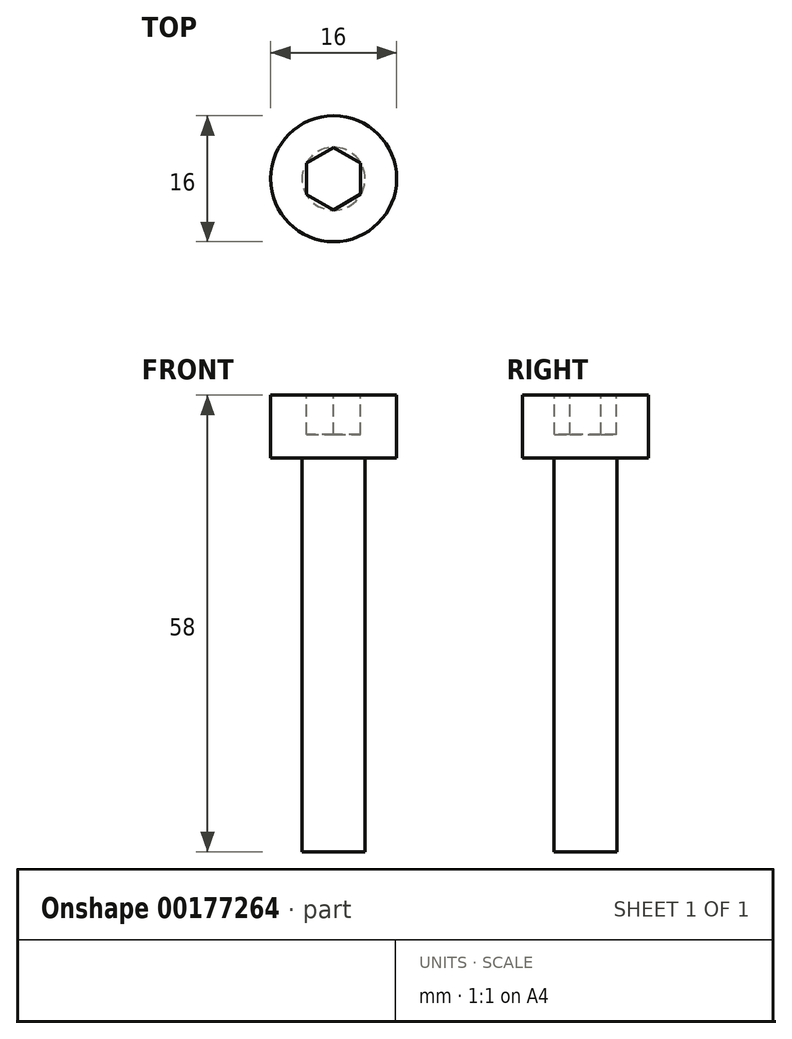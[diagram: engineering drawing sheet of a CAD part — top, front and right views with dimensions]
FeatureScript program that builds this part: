
annotation { "Feature Type Name" : "Feature", "Feature Type Description" : "" }
export const myFeature = defineFeature(function(context is Context, id is Id, definition is map)
    precondition{}
    {
        {
            var Q0;
            Q0=qCreatedBy(makeId("Top.planeOp"),FACE);
            var sketch = newSketch(context, id + "F0", { "sketchPlane" : qUnion([Q0])});
            skCircle(sketch, "E0", {"center": v(0, 0) * mm, "radius": 4 * mm});
            skCircle(sketch, "E1", {"center": v(0, 0) * mm, "radius": 8 * mm});
            skSolve(sketch);
        }
        {
            var Q0;
            Q0=makeQuery(id+"F0.imprint","IMPRINT",FACE,{"disambiguationData":[TD([[makeQuery(id+"F0.imprint","IMPRINT",EDGE,{"derivedFrom":sQuery(id+"F0.wireOp",EDGE,"E0")}),1.0]])]});
            extrude(context, id + "F1", {"entities" : qUnion([Q0]), "oppositeDirection" : true, "depth" : 50 * mm});
        }
        {
            var Q0;
            Q0=makeQuery(id+"F0.imprint","IMPRINT",FACE,{"disambiguationData":[TD([[makeQuery(id+"F0.imprint","IMPRINT",EDGE,{"derivedFrom":sQuery(id+"F0.wireOp",EDGE,"E0")}),-1.0]])]});
            var Q1;
            Q1=makeQuery(id+"F0.imprint","IMPRINT",FACE,{"disambiguationData":[TD([[makeQuery(id+"F0.imprint","IMPRINT",EDGE,{"derivedFrom":sQuery(id+"F0.wireOp",EDGE,"E0")}),1.0]])]});
            extrude(context, id + "F2", {"entities" : qUnion([Q0, Q1]), "operationType" : NewBodyOperationType.ADD, "depth" : 8 * mm});
        }
        {
            var Q0;
            Q0=makeQuery(id+"F2.opExtrude","CAP_FACE",FACE,{"disambiguationData":[OSD([sQuery(id+"F0.wireOp",EDGE,"E0"),sQuery(id+"F0.wireOp",EDGE,"E1")])],"isStart":false});
            var sketch = newSketch(context, id + "F3", { "sketchPlane" : qUnion([Q0])});
            skPoint(sketch, "E2.0", {"position": v(0, 0) * mm});
            skCircle(sketch, "E3", {"center": v(0, 0) * mm, "radius": 9.85 * mm});
            skCircle(sketch, "E4.cCircle", {"center": v(0, 0) * mm, "radius": 3.42 * mm, "construction": true});
            skLineSegment(sketch, "E4.0", {"start": v(-3.43, 1.97) * mm, "end": v(-0.01, 3.95) * mm});
            skLineSegment(sketch, "E4.1", {"start": v(-0.01, 3.95) * mm, "end": v(3.42, 1.99) * mm});
            skLineSegment(sketch, "E4.2", {"start": v(3.42, 1.99) * mm, "end": v(3.43, -1.97) * mm});
            skLineSegment(sketch, "E4.3", {"start": v(3.43, -1.97) * mm, "end": v(0.01, -3.95) * mm});
            skLineSegment(sketch, "E4.4", {"start": v(0.01, -3.95) * mm, "end": v(-3.42, -1.99) * mm});
            skLineSegment(sketch, "E4.5", {"start": v(-3.42, -1.99) * mm, "end": v(-3.43, 1.97) * mm});
            skPoint(sketch, "E4.0.midPoint", {"position": v(-1.72, 2.96) * mm});
            skSolve(sketch);
        }
        {
            var Q0;
            Q0=makeQuery(id+"F3.imprint","IMPRINT",FACE,{"disambiguationData":[TD([[makeQuery(id+"F3.imprint","IMPRINT",EDGE,{"derivedFrom":sQuery(id+"F3.wireOp",EDGE,"E4.0")}),-1.0]])]});
            var Q1;
            Q1=makeQuery(id+"F1.opExtrude","CAP_FACE",FACE,{"disambiguationData":[OSD([sQuery(id+"F0.wireOp",EDGE,"E0")])],"isStart":true});
            var Q2;
            Q2=makeQuery(id+"F1.opExtrude","SWEPT_BODY",BODY,{"disambiguationData":[OSD([sQuery(id+"F0.wireOp",EDGE,"E0")])]});
            extrude(context, id + "F4", {"entities" : qUnion([Q0]), "operationType" : NewBodyOperationType.REMOVE, "oppositeDirection" : true, "endBoundEntityFace" : qUnion([Q1]), "endBoundEntityBody" : qUnion([Q2]), "depth" : 5 * mm});
        }
    });
